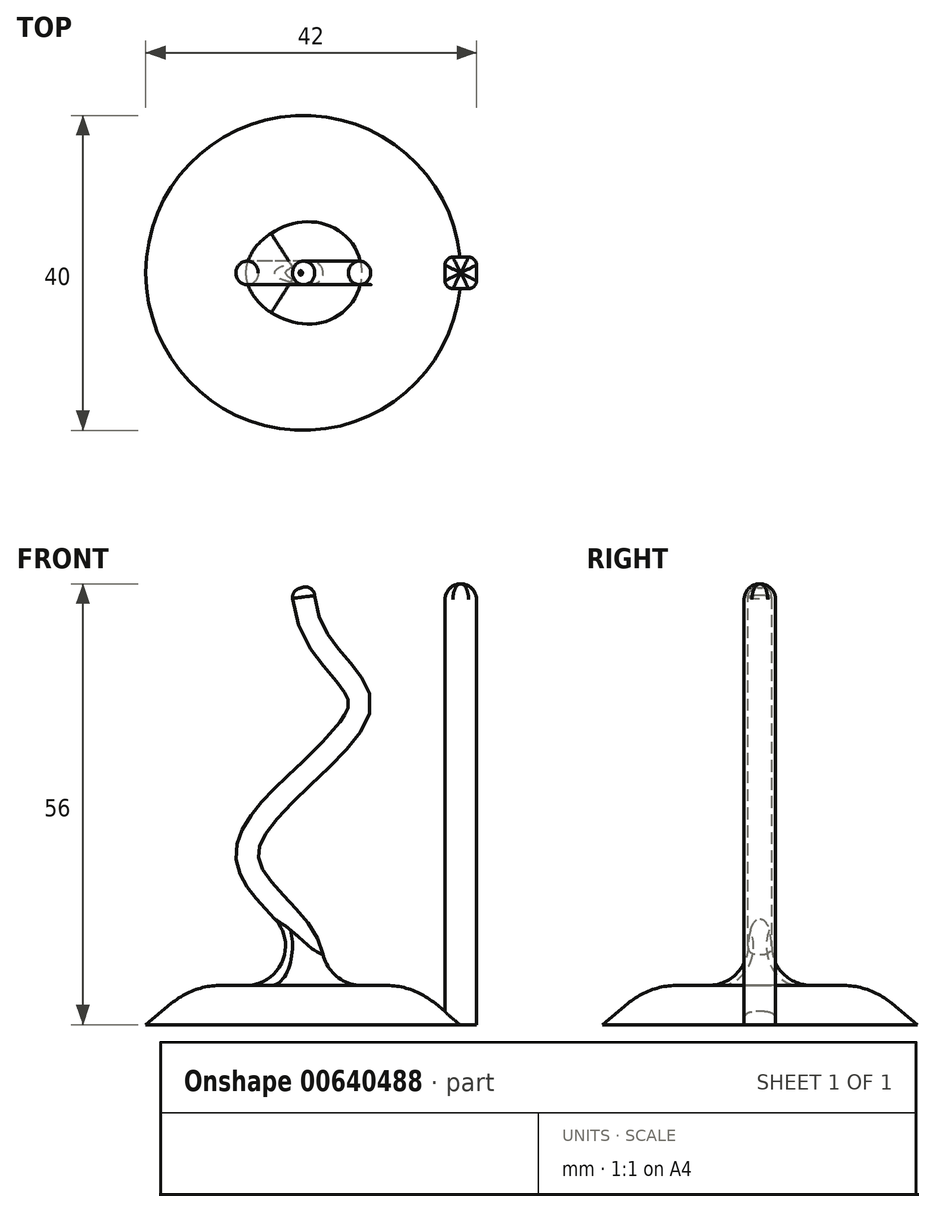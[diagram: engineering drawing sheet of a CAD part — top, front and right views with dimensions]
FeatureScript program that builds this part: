
annotation { "Feature Type Name" : "Feature", "Feature Type Description" : "" }
export const myFeature = defineFeature(function(context is Context, id is Id, definition is map)
    precondition{}
    {
        {
            var Q0;
            Q0=qCreatedBy(makeId("Top.planeOp"),FACE);
            var sketch = newSketch(context, id + "F0", { "sketchPlane" : qUnion([Q0])});
            skCircle(sketch, "E0", {"center": v(0, 0) * mm, "radius": 20 * mm});
            skSolve(sketch);
        }
        {
            var Q0;
            Q0=makeQuery(id+"F0.imprint","IMPRINT",FACE,{"disambiguationData":[TD([[makeQuery(id+"F0.imprint","IMPRINT",EDGE,{"derivedFrom":sQuery(id+"F0.wireOp",EDGE,"E0")}),1.0]])]});
            extrude(context, id + "F1", {"entities" : qUnion([Q0]), "depth" : 5 * mm, "offsetDistance" : 25 * mm});
        }
        {
            var Q0;
            Q0=makeQuery(id+"F1.opExtrude","CAP_EDGE",EDGE,{"disambiguationData":[OSD([sQuery(id+"F0.wireOp",EDGE,"E0")])],"isStart":false});
            chamfer(context, id + "F2", {"entities" : qUnion([Q0]), "chamferType" : ChamferType.TWO_OFFSETS, "width1" : 6 * mm, "oppositeDirection" : false, "width2" : 5 * mm, "tangentPropagation" : true});
        }
        {
            var Q0;
            Q0=qCreatedBy(makeId("Front.planeOp"),FACE);
            var sketch = newSketch(context, id + "F3", { "sketchPlane" : qUnion([Q0])});
            skFitSpline(sketch, "E1", {"points": [v(0, 0) * mm, v(0, 11.3) * mm, v(-7.02, 22.63) * mm, v(7.08, 40.24) * mm, v(0, 55.58) * mm], "startDerivative": vector(20.5, 62.19) * mm, "endDerivative": vector(0, 98.56) * mm});
            skSolve(sketch);
        }
        {
            var Q0;
            Q0=qCreatedBy(makeId("Top.planeOp"),FACE);
            var sketch = newSketch(context, id + "F4", { "sketchPlane" : qUnion([Q0])});
            skCircle(sketch, "E2", {"center": v(0, 0) * mm, "radius": 1.5 * mm});
            skSolve(sketch);
        }
        {
            var Q0;
            Q0 = qSketchRegion(id + "F4", true);
            var Q1;
            Q1 = qConstructionFilter(qBodyType(qCreatedBy(id + "F3" ,EDGE), BodyType.WIRE), ConstructionObject.NO);
            sweep(context, id + "F5", {"operationType" : NewBodyOperationType.ADD, "profiles" : qUnion([Q0]), "path" : qUnion([Q1])});
        }
        {
            var Q0;
            Q0=makeQuery(id+"F5.opSweep","CAP_EDGE",EDGE,{"disambiguationData":[OSD([sQuery(id+"F3.wireOp",VERTEX,"E1.end"),sQuery(id+"F4.wireOp",EDGE,"E2")])],"isStart":false});
            fillet(context, id + "F6", {"entities" : qUnion([Q0]), "radius" : 1.2 * mm, "tangentPropagation" : true, "allowEdgeOverflow" : false});
        }
        {
            var Q0;
            {var subQ0=sQuery(id+"F0.wireOp",EDGE,"E0");Q0=makeQuery(id+"F2.opChamfer","BLEND_EDGE",EDGE,{"blendedFrom":[makeQuery(id+"F1.opExtrude","CAP_EDGE",EDGE,{"disambiguationData":[OSD([subQ0])],"isStart":false}),makeQuery(id+"F1.opExtrude","CAP_FACE",FACE,{"disambiguationData":[OSD([subQ0])],"isStart":false})],"blendedInto":[makeQuery(id+"F1.opExtrude","CAP_FACE",FACE,{"disambiguationData":[OSD([subQ0])],"isStart":false})]});}
            fillet(context, id + "F7", {"entities" : qUnion([Q0]), "radius" : 10 * mm, "tangentPropagation" : true, "allowEdgeOverflow" : false});
        }
        {
            var Q0;
            Q0=makeQuery(id+"F5.boolean.opBoolean","INTERSECT",EDGE,{"derivedFrom":[makeQuery(id+"F1.opExtrude","CAP_FACE",FACE,{"disambiguationData":[OSD([sQuery(id+"F0.wireOp",EDGE,"E0")])],"isStart":false}),makeQuery(id+"F5.opSweep","SWEPT_FACE",FACE,{"disambiguationData":[OSD([sQuery(id+"F3.wireOp",EDGE,"E1"),sQuery(id+"F4.wireOp",EDGE,"E2")])]})]});
            fillet(context, id + "F8", {"entities" : qUnion([Q0]), "radius" : 5 * mm, "tangentPropagation" : true, "allowEdgeOverflow" : false});
        }
        {
            var Q0;
            Q0=qCreatedBy(makeId("Top.planeOp"),FACE);
            var sketch = newSketch(context, id + "F9", { "sketchPlane" : qUnion([Q0])});
            skLineSegment(sketch, "E3.bottom", {"start": v(22, -2) * mm, "end": v(18, -2) * mm});
            skLineSegment(sketch, "E3.top", {"start": v(22, 2) * mm, "end": v(18, 2) * mm});
            skLineSegment(sketch, "E3.left", {"start": v(22, -2) * mm, "end": v(22, 2) * mm});
            skLineSegment(sketch, "E3.right", {"start": v(18, -2) * mm, "end": v(18, 2) * mm});
            skPoint(sketch, "E3.middle", {"position": v(20, 0) * mm});
            skSolve(sketch);
        }
        {
            var Q0;
            Q0 = qSketchRegion(id + "F9", true);
            extrude(context, id + "F10", {"entities" : qUnion([Q0]), "operationType" : NewBodyOperationType.ADD, "depth" : 56 * mm, "offsetDistance" : 25 * mm});
        }
        {
            var Q0;
            Q0=makeQuery(id+"F10.opExtrude","CAP_EDGE",EDGE,{"disambiguationData":[OSD([sQuery(id+"F9.wireOp",EDGE,"E3.bottom")])],"isStart":false});
            var Q1;
            Q1=makeQuery(id+"F10.opExtrude","CAP_EDGE",EDGE,{"disambiguationData":[OSD([sQuery(id+"F9.wireOp",EDGE,"E3.right")])],"isStart":false});
            var Q2;
            Q2=makeQuery(id+"F10.opExtrude","CAP_EDGE",EDGE,{"disambiguationData":[OSD([sQuery(id+"F9.wireOp",EDGE,"E3.top")])],"isStart":false});
            var Q3;
            Q3=makeQuery(id+"F10.opExtrude","CAP_EDGE",EDGE,{"disambiguationData":[OSD([sQuery(id+"F9.wireOp",EDGE,"E3.left")])],"isStart":false});
            fillet(context, id + "F11", {"entities" : qUnion([Q0, Q1, Q2, Q3]), "radius" : 2 * mm, "tangentPropagation" : true, "allowEdgeOverflow" : false});
        }
        {
            var Q0;
            Q0=makeQuery(id+"F11.opFillet","BLEND_EDGE",EDGE,{"blendedFrom":[makeQuery(id+"F10.opExtrude","CAP_EDGE",EDGE,{"disambiguationData":[OSD([sQuery(id+"F9.wireOp",EDGE,"E3.bottom")])],"isStart":false}),makeQuery(id+"F10.opExtrude","CAP_EDGE",EDGE,{"disambiguationData":[OSD([sQuery(id+"F9.wireOp",EDGE,"E3.right")])],"isStart":false})],"blendedInto":[]});
            var Q1;
            Q1=makeQuery(id+"F11.opFillet","BLEND_EDGE",EDGE,{"blendedFrom":[makeQuery(id+"F10.opExtrude","CAP_EDGE",EDGE,{"disambiguationData":[OSD([sQuery(id+"F9.wireOp",EDGE,"E3.bottom")])],"isStart":false}),makeQuery(id+"F10.opExtrude","CAP_EDGE",EDGE,{"disambiguationData":[OSD([sQuery(id+"F9.wireOp",EDGE,"E3.left")])],"isStart":false})],"blendedInto":[]});
            var Q2;
            Q2=makeQuery(id+"F11.opFillet","BLEND_FACE",FACE,{"disambiguationData":[OSD([sQuery(id+"F9.wireOp",EDGE,"E3.left")])]});
            var Q3;
            Q3=makeQuery(id+"F11.opFillet","BLEND_EDGE",EDGE,{"blendedFrom":[makeQuery(id+"F10.opExtrude","CAP_EDGE",EDGE,{"disambiguationData":[OSD([sQuery(id+"F9.wireOp",EDGE,"E3.top")])],"isStart":false}),makeQuery(id+"F10.opExtrude","CAP_EDGE",EDGE,{"disambiguationData":[OSD([sQuery(id+"F9.wireOp",EDGE,"E3.right")])],"isStart":false})],"blendedInto":[]});
            fillet(context, id + "F12", {"entities" : qUnion([Q0, Q1, Q2, Q3]), "radius" : 1 * mm, "tangentPropagation" : true, "allowEdgeOverflow" : false});
        }
    });
